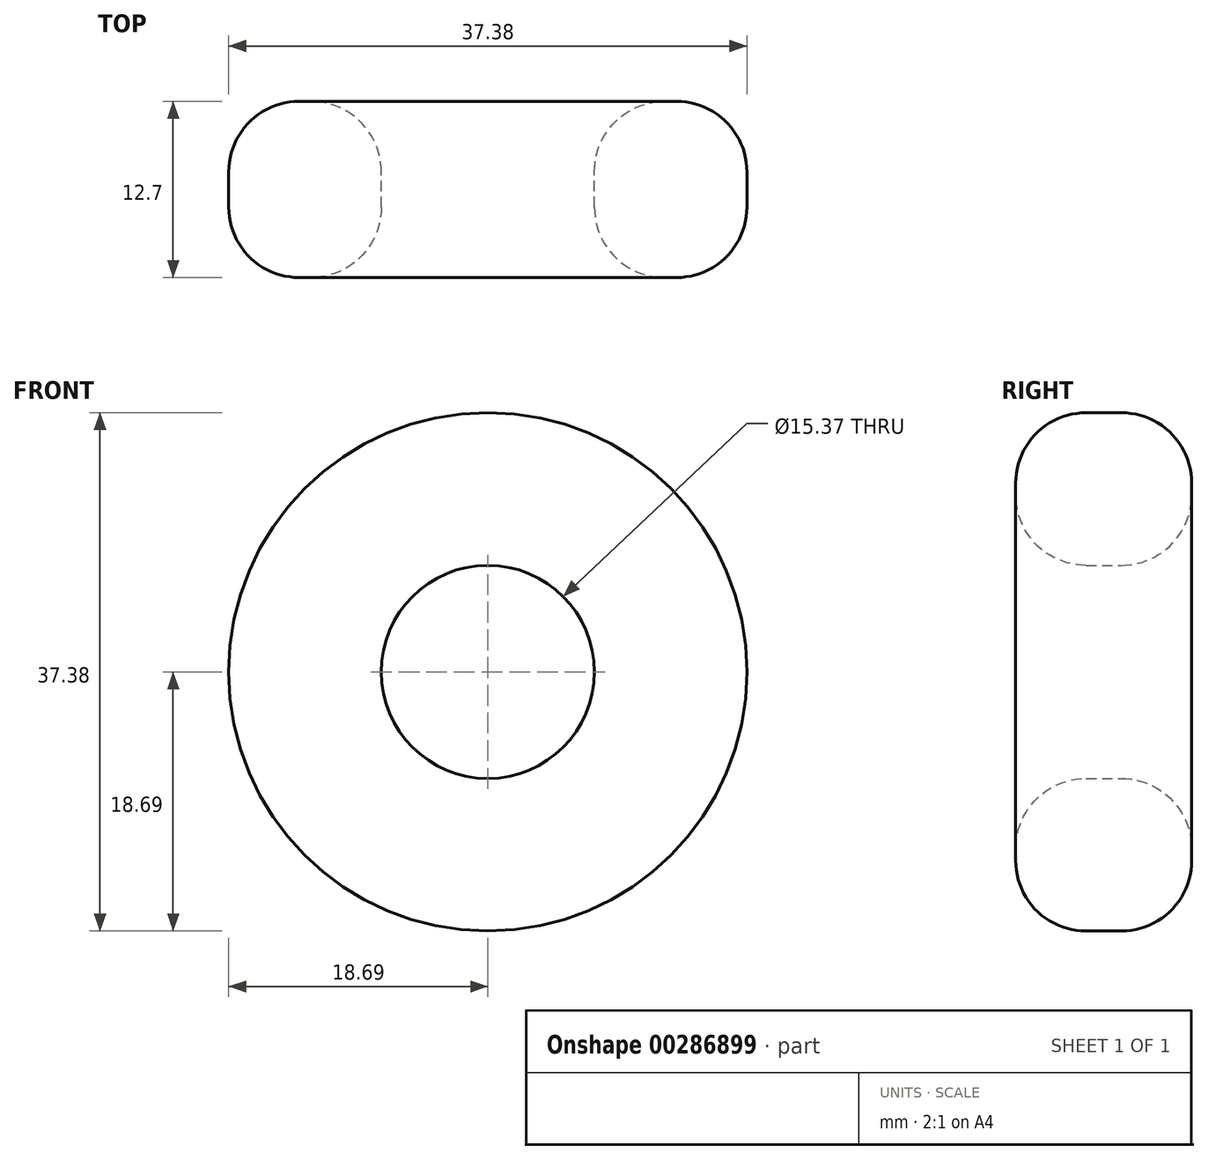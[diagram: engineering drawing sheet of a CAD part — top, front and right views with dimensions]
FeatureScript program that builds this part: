
annotation { "Feature Type Name" : "Feature", "Feature Type Description" : "" }
export const myFeature = defineFeature(function(context is Context, id is Id, definition is map)
    precondition{}
    {
        {
            var Q0;
            Q0=qCreatedBy(makeId("Front.planeOp"),FACE);
            var sketch = newSketch(context, id + "F0", { "sketchPlane" : qUnion([Q0])});
            skCircle(sketch, "E0", {"center": v(0, 0) * mm, "radius": 7.69 * mm});
            skCircle(sketch, "E1", {"center": v(0, 0) * mm, "radius": 18.7 * mm});
            skSolve(sketch);
        }
        {
            var Q0;
            Q0=makeQuery(id+"F0.imprint","IMPRINT",FACE,{"disambiguationData":[TD([[makeQuery(id+"F0.imprint","IMPRINT",EDGE,{"derivedFrom":sQuery(id+"F0.wireOp",EDGE,"E0")}),-1.0]])]});
            extrude(context, id + "F1", {"entities" : qUnion([Q0]), "depth" : 6.35 * mm});
        }
        {
            var Q0;
            Q0=makeQuery(id+"F1.opExtrude","CAP_FACE",FACE,{"disambiguationData":[OSD([sQuery(id+"F0.wireOp",EDGE,"E0"),sQuery(id+"F0.wireOp",EDGE,"E1")])],"isStart":false});
            fillet(context, id + "F2", {"entities" : qUnion([Q0]), "radius" : 5.08 * mm, "tangentPropagation" : true, "allowEdgeOverflow" : false});
        }
        {
            var Q0;
            Q0=makeQuery(id+"F1.opExtrude","CAP_FACE",FACE,{"disambiguationData":[OSD([sQuery(id+"F0.wireOp",EDGE,"E0"),sQuery(id+"F0.wireOp",EDGE,"E1")])],"isStart":true});
            extrude(context, id + "F3", {"entities" : qUnion([Q0]), "operationType" : NewBodyOperationType.ADD, "depth" : 6.35 * mm});
        }
        {
            var Q0;
            Q0=makeQuery(id+"F3.opExtrude","CAP_FACE",FACE,{"disambiguationData":[OSD([sQuery(id+"F0.wireOp",EDGE,"E0"),sQuery(id+"F0.wireOp",EDGE,"E1")])],"isStart":false});
            fillet(context, id + "F4", {"entities" : qUnion([Q0]), "radius" : 5.08 * mm, "tangentPropagation" : true, "allowEdgeOverflow" : false});
        }
    });
